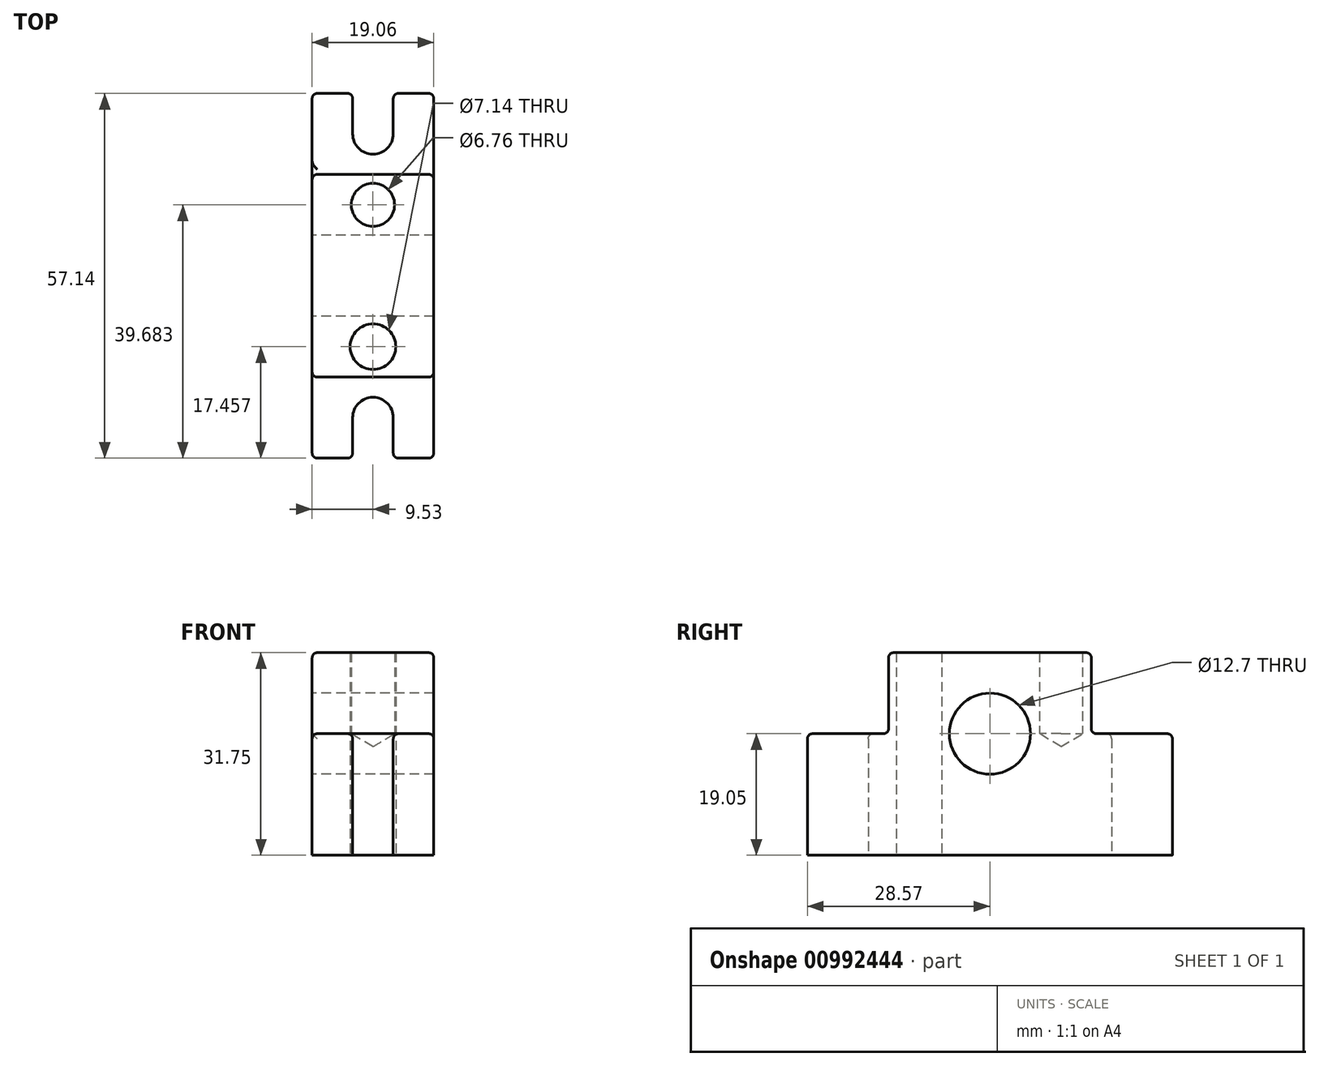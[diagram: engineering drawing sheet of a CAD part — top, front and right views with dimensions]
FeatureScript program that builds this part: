
annotation { "Feature Type Name" : "Feature", "Feature Type Description" : "" }
export const myFeature = defineFeature(function(context is Context, id is Id, definition is map)
    precondition{}
    {
        {
            var Q0;
            Q0=qCreatedBy(makeId("Top.planeOp"),FACE);
            var sketch = newSketch(context, id + "F0", { "sketchPlane" : qUnion([Q0])});
            skLineSegment(sketch, "E0.bottom", {"start": v(9.53, 28.58) * mm, "end": v(3.17, 28.58) * mm});
            skLineSegment(sketch, "E0.top", {"start": v(9.53, -28.58) * mm, "end": v(3.18, -28.58) * mm});
            skLineSegment(sketch, "E0.left", {"start": v(9.53, 28.58) * mm, "end": v(9.53, -28.58) * mm});
            skLineSegment(sketch, "E0.right", {"start": v(-9.52, 28.58) * mm, "end": v(-9.53, -28.58) * mm});
            skPoint(sketch, "E0.middle", {"position": v(0, 0) * mm});
            skArc(sketch, "E1", {"start": v(-3.18, 22.23) * mm, "mid": v(0, 19.05) * mm, "end": v(3.17, 22.23) * mm});
            skArc(sketch, "E2", {"start": v(3.18, -22.23) * mm, "mid": v(0, -19.05) * mm, "end": v(-3.18, -22.23) * mm});
            skLineSegment(sketch, "E3.left", {"start": v(3.18, -22.23) * mm, "end": v(3.18, -28.58) * mm});
            skLineSegment(sketch, "E3.right", {"start": v(-3.17, -22.23) * mm, "end": v(-3.17, -28.58) * mm});
            skLineSegment(sketch, "E4.trimOffspring", {"start": v(-3.17, -28.58) * mm, "end": v(-9.53, -28.58) * mm});
            skLineSegment(sketch, "E5.left", {"start": v(3.17, 28.58) * mm, "end": v(3.17, 22.23) * mm});
            skLineSegment(sketch, "E5.right", {"start": v(-3.18, 28.58) * mm, "end": v(-3.18, 22.23) * mm});
            skLineSegment(sketch, "E6.trimOffspring", {"start": v(-3.18, 28.58) * mm, "end": v(-9.52, 28.58) * mm});
            skLineSegment(sketch, "E7.bottom", {"start": v(-9.53, -15.88) * mm, "end": v(9.53, -15.88) * mm});
            skLineSegment(sketch, "E7.top", {"start": v(-9.53, 15.88) * mm, "end": v(9.53, 15.88) * mm});
            skLineSegment(sketch, "E7.left", {"start": v(-9.53, -15.88) * mm, "end": v(-9.53, 15.88) * mm});
            skLineSegment(sketch, "E7.right", {"start": v(9.53, -15.88) * mm, "end": v(9.53, 15.88) * mm});
            skLineSegment(sketch, "E8.bottom", {"start": v(-9.53, 0) * mm, "end": v(9.53, 0) * mm});
            skLineSegment(sketch, "E8.top", {"start": v(-9.53, 6.35) * mm, "end": v(9.53, 6.35) * mm});
            skLineSegment(sketch, "E8.left", {"start": v(-9.53, 0) * mm, "end": v(-9.53, 6.35) * mm});
            skLineSegment(sketch, "E8.right", {"start": v(9.53, 0) * mm, "end": v(9.53, 6.35) * mm});
            skCircle(sketch, "E9", {"center": v(0, 11.11) * mm, "radius": 3.57 * mm});
            skCircle(sketch, "E10.MirrorC", {"center": v(0, -11.11) * mm, "radius": 3.57 * mm});
            skSolve(sketch);
        }
        {
            var Q0;
            {var subQ0=sQuery(id+"F0.wireOp",EDGE,"E8.bottom");Q0=makeQuery(id+"F0.imprint","IMPRINT",FACE,{"disambiguationData":[TD([[makeQuery(id+"F0.imprint","IMPRINT",EDGE,{"derivedFrom":subQ0}),1.0]])]});}
            var Q1;
            {var subQ4=sQuery(id+"F0.wireOp",EDGE,"E0.top");Q1=makeQuery(id+"F0.imprint","IMPRINT",FACE,{"disambiguationData":[TD([[makeQuery(id+"F0.imprint","IMPRINT",EDGE,{"derivedFrom":subQ4}),-1.0]])]});}
            var Q2;
            {var subQ0=sQuery(id+"F0.wireOp",EDGE,"E7.bottom");Q2=makeQuery(id+"F0.imprint","IMPRINT",FACE,{"disambiguationData":[TD([[makeQuery(id+"F0.imprint","IMPRINT",EDGE,{"derivedFrom":subQ0}),1.0]])]});}
            var Q3;
            {var subQ1=sQuery(id+"F0.wireOp",EDGE,"E7.top");Q3=makeQuery(id+"F0.imprint","IMPRINT",FACE,{"disambiguationData":[TD([[makeQuery(id+"F0.imprint","IMPRINT",EDGE,{"derivedFrom":subQ1}),-1.0]])]});}
            var Q4;
            {var subQ4=sQuery(id+"F0.wireOp",EDGE,"E0.bottom");Q4=makeQuery(id+"F0.imprint","IMPRINT",FACE,{"disambiguationData":[TD([[makeQuery(id+"F0.imprint","IMPRINT",EDGE,{"derivedFrom":subQ4}),1.0]])]});}
            var Q5;
            Q5=makeQuery(id+"F0.imprint","IMPRINT",FACE,{"disambiguationData":[TD([[makeQuery(id+"F0.imprint","IMPRINT",EDGE,{"derivedFrom":sQuery(id+"F0.wireOp",EDGE,"E9")}),1.0]])]});
            var Q6;
            Q6=makeQuery(id+"F0.imprint","IMPRINT",FACE,{"disambiguationData":[TD([[makeQuery(id+"F0.imprint","IMPRINT",EDGE,{"derivedFrom":sQuery(id+"F0.wireOp",EDGE,"E10.MirrorC")}),-1.0]])]});
            extrude(context, id + "F1", {"entities" : qUnion([Q0, Q1, Q2, Q3, Q4, Q5, Q6]), "depth" : 19.05 * mm, "offsetDistance" : 25.4 * mm});
        }
        {
            var Q0;
            {var subQ0=sQuery(id+"F0.wireOp",EDGE,"E8.bottom");Q0=makeQuery(id+"F0.imprint","IMPRINT",FACE,{"disambiguationData":[TD([[makeQuery(id+"F0.imprint","IMPRINT",EDGE,{"derivedFrom":subQ0}),1.0]])]});}
            var Q1;
            {var subQ0=sQuery(id+"F0.wireOp",EDGE,"E7.bottom");Q1=makeQuery(id+"F0.imprint","IMPRINT",FACE,{"disambiguationData":[TD([[makeQuery(id+"F0.imprint","IMPRINT",EDGE,{"derivedFrom":subQ0}),1.0]])]});}
            var Q2;
            {var subQ1=sQuery(id+"F0.wireOp",EDGE,"E7.top");Q2=makeQuery(id+"F0.imprint","IMPRINT",FACE,{"disambiguationData":[TD([[makeQuery(id+"F0.imprint","IMPRINT",EDGE,{"derivedFrom":subQ1}),-1.0]])]});}
            var Q3;
            Q3=makeQuery(id+"F0.imprint","IMPRINT",FACE,{"disambiguationData":[TD([[makeQuery(id+"F0.imprint","IMPRINT",EDGE,{"derivedFrom":sQuery(id+"F0.wireOp",EDGE,"E10.MirrorC")}),-1.0]])]});
            var Q4;
            Q4=makeQuery(id+"F0.imprint","IMPRINT",FACE,{"disambiguationData":[TD([[makeQuery(id+"F0.imprint","IMPRINT",EDGE,{"derivedFrom":sQuery(id+"F0.wireOp",EDGE,"E9")}),1.0]])]});
            extrude(context, id + "F2", {"entities" : qUnion([Q0, Q1, Q2, Q3, Q4]), "operationType" : NewBodyOperationType.ADD, "depth" : 31.75 * mm, "offsetDistance" : 25.4 * mm});
        }
        {
            var Q0;
            {var subQ0=sQuery(id+"F0.wireOp",EDGE,"E0.left");Q0=makeQuery(id+"F2.boolean.opBoolean","MERGE",FACE,{"derivedFrom":[makeQuery(id+"F1.opExtrude","SWEPT_FACE",FACE,{"disambiguationData":[OSD([subQ0])]}),makeQuery(id+"F2.opExtrude","SWEPT_FACE",FACE,{"disambiguationData":[OSD([subQ0])]})]});}
            var sketch = newSketch(context, id + "F3", { "sketchPlane" : qUnion([Q0])});
            skCircle(sketch, "E11", {"center": v(0, 19.05) * mm, "radius": 6.35 * mm});
            skSolve(sketch);
        }
        {
            var Q0;
            Q0=sQuery(id+"F3.wireOp",VERTEX,"E11.center");
            var Q1;
            Q1=makeQuery(id+"F1.opExtrude","SWEPT_BODY",BODY,{"disambiguationData":[OSD([sQuery(id+"F0.wireOp",EDGE,"E0.bottom"),sQuery(id+"F0.wireOp",EDGE,"E0.top"),sQuery(id+"F0.wireOp",EDGE,"E0.left"),sQuery(id+"F0.wireOp",EDGE,"E0.right"),sQuery(id+"F0.wireOp",EDGE,"E1"),sQuery(id+"F0.wireOp",EDGE,"E2"),sQuery(id+"F0.wireOp",EDGE,"E3.left"),sQuery(id+"F0.wireOp",EDGE,"E3.right"),sQuery(id+"F0.wireOp",EDGE,"E4.trimOffspring"),sQuery(id+"F0.wireOp",EDGE,"E5.left"),sQuery(id+"F0.wireOp",EDGE,"E5.right"),sQuery(id+"F0.wireOp",EDGE,"E6.trimOffspring")])]});
            hole(context, id + "F4", {"style" : HoleStyle.SIMPLE, "endStyle" : HoleEndStyle.THROUGH, "holeDiameter" : 12.7 * mm, "majorDiameter" : 6.35 * mm, "isTappedThrough" : true, "tappedDepth" : 12.7 * mm, "tapClearance" : 3, "locations" : qUnion([Q0]), "scope" : qUnion([Q1]), "startStyle" : HoleStartStyle.SKETCH});
        }
        {
            var Q0;
            Q0=makeQuery(id+"F2.opExtrude","CAP_FACE",FACE,{"disambiguationData":[OSD([sQuery(id+"F0.wireOp",EDGE,"E0.left"),sQuery(id+"F0.wireOp",EDGE,"E0.right"),sQuery(id+"F0.wireOp",EDGE,"E7.bottom"),sQuery(id+"F0.wireOp",EDGE,"E7.top")])],"isStart":false});
            var sketch = newSketch(context, id + "F5", { "sketchPlane" : qUnion([Q0])});
            skCircle(sketch, "E12", {"center": v(0, 11.11) * mm, "radius": 3.57 * mm});
            skCircle(sketch, "E13", {"center": v(0, -11.11) * mm, "radius": 3.57 * mm});
            skSolve(sketch);
        }
        {
            var Q0;
            Q0=sQuery(id+"F5.wireOp",VERTEX,"E12.center");
            var Q1;
            Q1=sQuery(id+"F5.wireOp",VERTEX,"E13.center");
            var Q2;
            Q2=makeQuery(id+"F1.opExtrude","SWEPT_BODY",BODY,{"disambiguationData":[OSD([sQuery(id+"F0.wireOp",EDGE,"E0.bottom"),sQuery(id+"F0.wireOp",EDGE,"E0.top"),sQuery(id+"F0.wireOp",EDGE,"E0.left"),sQuery(id+"F0.wireOp",EDGE,"E0.right"),sQuery(id+"F0.wireOp",EDGE,"E1"),sQuery(id+"F0.wireOp",EDGE,"E2"),sQuery(id+"F0.wireOp",EDGE,"E3.left"),sQuery(id+"F0.wireOp",EDGE,"E3.right"),sQuery(id+"F0.wireOp",EDGE,"E4.trimOffspring"),sQuery(id+"F0.wireOp",EDGE,"E5.left"),sQuery(id+"F0.wireOp",EDGE,"E5.right"),sQuery(id+"F0.wireOp",EDGE,"E6.trimOffspring")])]});
            hole(context, id + "F6", {"style" : HoleStyle.SIMPLE, "endStyle" : HoleEndStyle.BLIND, "standardTappedOrClearance" : lookupTablePath({ "fit" : "Close (ASME)", "standard" : "ANSI", "size" : "1/4", "type" : "Clearance" }), "standardBlindInLast" : lookupTablePath({ "fit" : "Close", "standard" : "ANSI", "engagement" : "75%", "pitch" : "20 tpi", "size" : "1/4", "type" : "Clearance & tapped" }), "holeDiameter" : 6.76 * mm, "majorDiameter" : 6.35 * mm, "holeDepth" : 12.7 * mm, "isTappedThrough" : true, "tappedDepth" : 12.7 * mm, "tapClearance" : 3, "locations" : qUnion([Q0, Q1]), "scope" : qUnion([Q2]), "startStyle" : HoleStartStyle.SKETCH});
        }
        {
            var Q0;
            Q0=makeQuery(id+"F2.opExtrude","CAP_EDGE",EDGE,{"disambiguationData":[OSD([sQuery(id+"F0.wireOp",EDGE,"E0.right")])],"isStart":false});
            var Q1;
            Q1=makeQuery(id+"F2.opExtrude","CAP_EDGE",EDGE,{"disambiguationData":[OSD([sQuery(id+"F0.wireOp",EDGE,"E7.bottom")])],"isStart":false});
            var Q2;
            Q2=makeQuery(id+"F2.opExtrude","CAP_EDGE",EDGE,{"disambiguationData":[OSD([sQuery(id+"F0.wireOp",EDGE,"E0.left")])],"isStart":false});
            var Q3;
            Q3=makeQuery(id+"F2.opExtrude","CAP_EDGE",EDGE,{"disambiguationData":[OSD([sQuery(id+"F0.wireOp",EDGE,"E7.top")])],"isStart":false});
            var Q4;
            Q4=makeQuery(id+"F2.opExtrude","SWEPT_EDGE",EDGE,{"disambiguationData":[OSD([sQuery(id+"F0.wireOp",EDGE,"E0.left"),sQuery(id+"F0.wireOp",EDGE,"E7.top")])]});
            var Q5;
            Q5=makeQuery(id+"F2.opExtrude","SWEPT_EDGE",EDGE,{"disambiguationData":[OSD([sQuery(id+"F0.wireOp",EDGE,"E0.right"),sQuery(id+"F0.wireOp",EDGE,"E7.top")])]});
            var Q6;
            Q6=makeQuery(id+"F2.boolean.opBoolean","INTERSECT",EDGE,{"derivedFrom":[makeQuery(id+"F1.opExtrude","CAP_FACE",FACE,{"disambiguationData":[OSD([sQuery(id+"F0.wireOp",EDGE,"E0.bottom"),sQuery(id+"F0.wireOp",EDGE,"E0.top"),sQuery(id+"F0.wireOp",EDGE,"E0.left"),sQuery(id+"F0.wireOp",EDGE,"E0.right"),sQuery(id+"F0.wireOp",EDGE,"E1"),sQuery(id+"F0.wireOp",EDGE,"E2"),sQuery(id+"F0.wireOp",EDGE,"E3.left"),sQuery(id+"F0.wireOp",EDGE,"E3.right"),sQuery(id+"F0.wireOp",EDGE,"E4.trimOffspring"),sQuery(id+"F0.wireOp",EDGE,"E5.left"),sQuery(id+"F0.wireOp",EDGE,"E5.right"),sQuery(id+"F0.wireOp",EDGE,"E6.trimOffspring")])],"isStart":false}),makeQuery(id+"F2.opExtrude","SWEPT_FACE",FACE,{"disambiguationData":[OSD([sQuery(id+"F0.wireOp",EDGE,"E7.top")])]})]});
            var Q7;
            {var subQ0=sQuery(id+"F0.wireOp",EDGE,"E0.left");var subQ1=sQuery(id+"F0.wireOp",EDGE,"E0.bottom");Q7=makeQuery(id+"F2.boolean.opBoolean","SPLIT",EDGE,{"disambiguationData":[TD([makeQuery(id+"F1.opExtrude","SWEPT_FACE",FACE,{"disambiguationData":[OSD([subQ1])]})])],"derivedFrom":makeQuery(id+"F1.opExtrude","CAP_EDGE",EDGE,{"disambiguationData":[OSD([subQ0])],"isStart":false})});}
            var Q8;
            Q8=makeQuery(id+"F1.opExtrude","SWEPT_EDGE",EDGE,{"disambiguationData":[OSD([sQuery(id+"F0.wireOp",EDGE,"E0.bottom"),sQuery(id+"F0.wireOp",EDGE,"E0.left")])]});
            var Q9;
            Q9=makeQuery(id+"F1.opExtrude","SWEPT_EDGE",EDGE,{"disambiguationData":[OSD([sQuery(id+"F0.wireOp",EDGE,"E0.right"),sQuery(id+"F0.wireOp",EDGE,"E6.trimOffspring")])]});
            var Q10;
            Q10=makeQuery(id+"F1.opExtrude","CAP_EDGE",EDGE,{"disambiguationData":[OSD([sQuery(id+"F0.wireOp",EDGE,"E0.bottom")])],"isStart":false});
            var Q11;
            Q11=makeQuery(id+"F1.opExtrude","CAP_EDGE",EDGE,{"disambiguationData":[OSD([sQuery(id+"F0.wireOp",EDGE,"E6.trimOffspring")])],"isStart":false});
            var Q12;
            Q12=makeQuery(id+"F1.opExtrude","SWEPT_EDGE",EDGE,{"disambiguationData":[OSD([sQuery(id+"F0.wireOp",EDGE,"E0.bottom"),sQuery(id+"F0.wireOp",EDGE,"E5.left")])]});
            var Q13;
            Q13=makeQuery(id+"F1.opExtrude","SWEPT_EDGE",EDGE,{"disambiguationData":[OSD([sQuery(id+"F0.wireOp",EDGE,"E5.right"),sQuery(id+"F0.wireOp",EDGE,"E6.trimOffspring")])]});
            var Q14;
            Q14=makeQuery(id+"F1.opExtrude","CAP_EDGE",EDGE,{"disambiguationData":[OSD([sQuery(id+"F0.wireOp",EDGE,"E5.left")])],"isStart":false});
            var Q15;
            Q15=makeQuery(id+"F2.boolean.opBoolean","INTERSECT",EDGE,{"derivedFrom":[makeQuery(id+"F1.opExtrude","CAP_FACE",FACE,{"disambiguationData":[OSD([sQuery(id+"F0.wireOp",EDGE,"E0.bottom"),sQuery(id+"F0.wireOp",EDGE,"E0.top"),sQuery(id+"F0.wireOp",EDGE,"E0.left"),sQuery(id+"F0.wireOp",EDGE,"E0.right"),sQuery(id+"F0.wireOp",EDGE,"E1"),sQuery(id+"F0.wireOp",EDGE,"E2"),sQuery(id+"F0.wireOp",EDGE,"E3.left"),sQuery(id+"F0.wireOp",EDGE,"E3.right"),sQuery(id+"F0.wireOp",EDGE,"E4.trimOffspring"),sQuery(id+"F0.wireOp",EDGE,"E5.left"),sQuery(id+"F0.wireOp",EDGE,"E5.right"),sQuery(id+"F0.wireOp",EDGE,"E6.trimOffspring")])],"isStart":false}),makeQuery(id+"F2.opExtrude","SWEPT_FACE",FACE,{"disambiguationData":[OSD([sQuery(id+"F0.wireOp",EDGE,"E7.bottom")])]})]});
            var Q16;
            Q16=makeQuery(id+"F2.opExtrude","SWEPT_EDGE",EDGE,{"disambiguationData":[OSD([sQuery(id+"F0.wireOp",EDGE,"E0.left"),sQuery(id+"F0.wireOp",EDGE,"E7.bottom")])]});
            var Q17;
            {var subQ0=sQuery(id+"F0.wireOp",EDGE,"E0.left");var subQ1=sQuery(id+"F0.wireOp",EDGE,"E0.top");Q17=makeQuery(id+"F2.boolean.opBoolean","SPLIT",EDGE,{"disambiguationData":[TD([makeQuery(id+"F1.opExtrude","SWEPT_FACE",FACE,{"disambiguationData":[OSD([subQ1])]})])],"derivedFrom":makeQuery(id+"F1.opExtrude","CAP_EDGE",EDGE,{"disambiguationData":[OSD([subQ0])],"isStart":false})});}
            var Q18;
            {var subQ0=sQuery(id+"F0.wireOp",EDGE,"E0.right");var subQ1=sQuery(id+"F0.wireOp",EDGE,"E4.trimOffspring");Q18=makeQuery(id+"F2.boolean.opBoolean","SPLIT",EDGE,{"disambiguationData":[TD([makeQuery(id+"F1.opExtrude","SWEPT_FACE",FACE,{"disambiguationData":[OSD([subQ1])]})])],"derivedFrom":makeQuery(id+"F1.opExtrude","CAP_EDGE",EDGE,{"disambiguationData":[OSD([subQ0])],"isStart":false})});}
            var Q19;
            Q19=makeQuery(id+"F2.opExtrude","SWEPT_EDGE",EDGE,{"disambiguationData":[OSD([sQuery(id+"F0.wireOp",EDGE,"E0.right"),sQuery(id+"F0.wireOp",EDGE,"E7.bottom")])]});
            var Q20;
            Q20=makeQuery(id+"F1.opExtrude","CAP_EDGE",EDGE,{"disambiguationData":[OSD([sQuery(id+"F0.wireOp",EDGE,"E3.right")])],"isStart":false});
            var Q21;
            Q21=makeQuery(id+"F1.opExtrude","CAP_EDGE",EDGE,{"disambiguationData":[OSD([sQuery(id+"F0.wireOp",EDGE,"E0.top")])],"isStart":false});
            var Q22;
            Q22=makeQuery(id+"F1.opExtrude","CAP_EDGE",EDGE,{"disambiguationData":[OSD([sQuery(id+"F0.wireOp",EDGE,"E4.trimOffspring")])],"isStart":false});
            var Q23;
            Q23=makeQuery(id+"F1.opExtrude","SWEPT_EDGE",EDGE,{"disambiguationData":[OSD([sQuery(id+"F0.wireOp",EDGE,"E0.top"),sQuery(id+"F0.wireOp",EDGE,"E0.left")])]});
            var Q24;
            Q24=makeQuery(id+"F1.opExtrude","SWEPT_EDGE",EDGE,{"disambiguationData":[OSD([sQuery(id+"F0.wireOp",EDGE,"E0.right"),sQuery(id+"F0.wireOp",EDGE,"E4.trimOffspring")])]});
            var Q25;
            Q25=makeQuery(id+"F1.opExtrude","SWEPT_EDGE",EDGE,{"disambiguationData":[OSD([sQuery(id+"F0.wireOp",EDGE,"E0.top"),sQuery(id+"F0.wireOp",EDGE,"E3.left")])]});
            var Q26;
            Q26=makeQuery(id+"F1.opExtrude","SWEPT_EDGE",EDGE,{"disambiguationData":[OSD([sQuery(id+"F0.wireOp",EDGE,"E3.right"),sQuery(id+"F0.wireOp",EDGE,"E4.trimOffspring")])]});
            fillet(context, id + "F7", {"entities" : qUnion([Q0, Q1, Q2, Q3, Q4, Q5, Q6, Q7, Q8, Q9, Q10, Q11, Q12, Q13, Q14, Q15, Q16, Q17, Q18, Q19, Q20, Q21, Q22, Q23, Q24, Q25, Q26]), "radius" : 0.8 * mm, "tangentPropagation" : true, "allowEdgeOverflow" : false});
        }
    });
